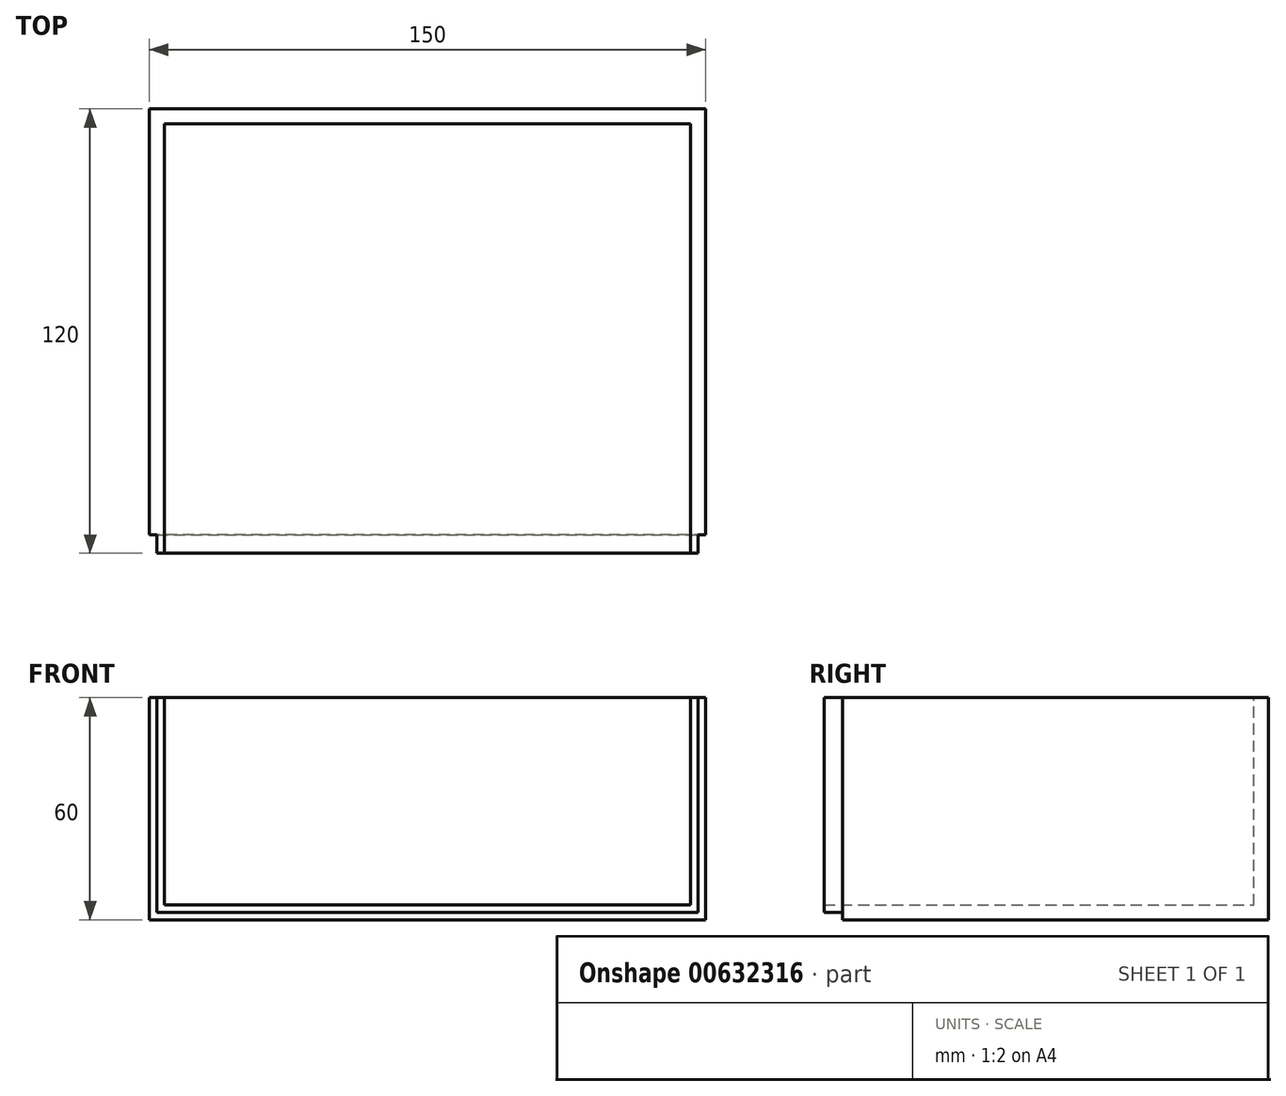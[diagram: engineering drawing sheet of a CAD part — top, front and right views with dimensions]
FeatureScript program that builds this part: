
annotation { "Feature Type Name" : "Feature", "Feature Type Description" : "" }
export const myFeature = defineFeature(function(context is Context, id is Id, definition is map)
    precondition{}
    {
        {
            var Q0;
            Q0=qCreatedBy(makeId("Right.planeOp"),FACE);
            var sketch = newSketch(context, id + "F0", { "sketchPlane" : qUnion([Q0])});
            skLineSegment(sketch, "E0.bottom", {"start": v(0, 0) * mm, "end": v(-120, 0) * mm});
            skLineSegment(sketch, "E0.top", {"start": v(0, 60) * mm, "end": v(-120, 60) * mm});
            skLineSegment(sketch, "E0.left", {"start": v(0, 0) * mm, "end": v(0, 60) * mm});
            skLineSegment(sketch, "E0.right", {"start": v(-120, 0) * mm, "end": v(-120, 60) * mm});
            skSolve(sketch);
        }
        {
            var Q0;
            Q0=makeQuery(id+"F0.imprint","IMPRINT",FACE,{"disambiguationData":[TD([[makeQuery(id+"F0.imprint","IMPRINT",EDGE,{"derivedFrom":sQuery(id+"F0.wireOp",EDGE,"E0.bottom")}),-1.0]])]});
            extrude(context, id + "F1", {"entities" : qUnion([Q0]), "oppositeDirection" : true, "depth" : 150 * mm, "offsetDistance" : 25 * mm});
        }
        {
            var Q0;
            Q0=makeQuery(id+"F1.opExtrude","SWEPT_FACE",FACE,{"disambiguationData":[OSD([sQuery(id+"F0.wireOp",EDGE,"E0.top")])]});
            var sketch = newSketch(context, id + "F2", { "sketchPlane" : qUnion([Q0])});
            skLineSegment(sketch, "E1.bottom", {"start": v(-146, -120) * mm, "end": v(-4, -120) * mm});
            skLineSegment(sketch, "E1.top", {"start": v(-146, -4) * mm, "end": v(-4, -4) * mm});
            skLineSegment(sketch, "E1.left", {"start": v(-146, -120) * mm, "end": v(-146, -4) * mm});
            skLineSegment(sketch, "E1.right", {"start": v(-4, -120) * mm, "end": v(-4, -4) * mm});
            skSolve(sketch);
        }
        {
            var Q0;
            Q0=makeQuery(id+"F2.imprint","IMPRINT",FACE,{"disambiguationData":[TD([[makeQuery(id+"F2.imprint","IMPRINT",EDGE,{"derivedFrom":sQuery(id+"F2.wireOp",EDGE,"E1.bottom")}),1.0]])]});
            extrude(context, id + "F3", {"entities" : qUnion([Q0]), "operationType" : NewBodyOperationType.REMOVE, "oppositeDirection" : true, "depth" : 56 * mm, "offsetDistance" : 25 * mm});
        }
        {
            var Q0;
            Q0=makeQuery(id+"F1.opExtrude","CAP_FACE",FACE,{"disambiguationData":[OSD([sQuery(id+"F0.wireOp",EDGE,"E0.bottom"),sQuery(id+"F0.wireOp",EDGE,"E0.top"),sQuery(id+"F0.wireOp",EDGE,"E0.left"),sQuery(id+"F0.wireOp",EDGE,"E0.right")])],"isStart":false});
            var sketch = newSketch(context, id + "F4", { "sketchPlane" : qUnion([Q0])});
            skLineSegment(sketch, "E2.bottom", {"start": v(120, 0) * mm, "end": v(115, 0) * mm});
            skLineSegment(sketch, "E2.top", {"start": v(120, 60) * mm, "end": v(115, 60) * mm});
            skLineSegment(sketch, "E2.left", {"start": v(120, 0) * mm, "end": v(120, 60) * mm});
            skLineSegment(sketch, "E2.right", {"start": v(115, 0) * mm, "end": v(115, 60) * mm});
            skSolve(sketch);
        }
        {
            var Q0;
            Q0 = qSketchRegion(id + "F4", true);
            extrude(context, id + "F5", {"entities" : qUnion([Q0]), "operationType" : NewBodyOperationType.REMOVE, "oppositeDirection" : true, "depth" : 2 * mm, "offsetDistance" : 25 * mm});
        }
        {
            var Q0;
            Q0=makeQuery(id+"F1.opExtrude","CAP_FACE",FACE,{"disambiguationData":[OSD([sQuery(id+"F0.wireOp",EDGE,"E0.bottom"),sQuery(id+"F0.wireOp",EDGE,"E0.top"),sQuery(id+"F0.wireOp",EDGE,"E0.left"),sQuery(id+"F0.wireOp",EDGE,"E0.right")])],"isStart":true});
            var sketch = newSketch(context, id + "F6", { "sketchPlane" : qUnion([Q0])});
            skLineSegment(sketch, "E3.bottom", {"start": v(-120, 0) * mm, "end": v(-115, 0) * mm});
            skLineSegment(sketch, "E3.top", {"start": v(-120, 60) * mm, "end": v(-115, 60) * mm});
            skLineSegment(sketch, "E3.left", {"start": v(-120, 0) * mm, "end": v(-120, 60) * mm});
            skLineSegment(sketch, "E3.right", {"start": v(-115, 0) * mm, "end": v(-115, 60) * mm});
            skSolve(sketch);
        }
        {
            var Q0;
            Q0 = qSketchRegion(id + "F6", true);
            extrude(context, id + "F7", {"entities" : qUnion([Q0]), "operationType" : NewBodyOperationType.REMOVE, "oppositeDirection" : true, "depth" : 2 * mm, "offsetDistance" : 25 * mm});
        }
        {
            var Q0;
            Q0=makeQuery(id+"F1.opExtrude","SWEPT_FACE",FACE,{"disambiguationData":[OSD([sQuery(id+"F0.wireOp",EDGE,"E0.bottom")])]});
            var sketch = newSketch(context, id + "F8", { "sketchPlane" : qUnion([Q0])});
            skLineSegment(sketch, "E4.bottom", {"start": v(-148, 120) * mm, "end": v(-2, 120) * mm});
            skLineSegment(sketch, "E4.top", {"start": v(-148, 115) * mm, "end": v(-2, 115) * mm});
            skLineSegment(sketch, "E4.left", {"start": v(-148, 120) * mm, "end": v(-148, 115) * mm});
            skLineSegment(sketch, "E4.right", {"start": v(-2, 120) * mm, "end": v(-2, 115) * mm});
            skSolve(sketch);
        }
        {
            var Q0;
            Q0=makeQuery(id+"F8.imprint","IMPRINT",FACE,{"disambiguationData":[TD([[makeQuery(id+"F8.imprint","IMPRINT",EDGE,{"derivedFrom":sQuery(id+"F8.wireOp",EDGE,"E4.bottom")}),-1.0]])]});
            extrude(context, id + "F9", {"entities" : qUnion([Q0]), "operationType" : NewBodyOperationType.REMOVE, "oppositeDirection" : true, "depth" : 2 * mm, "offsetDistance" : 25 * mm});
        }
    });
